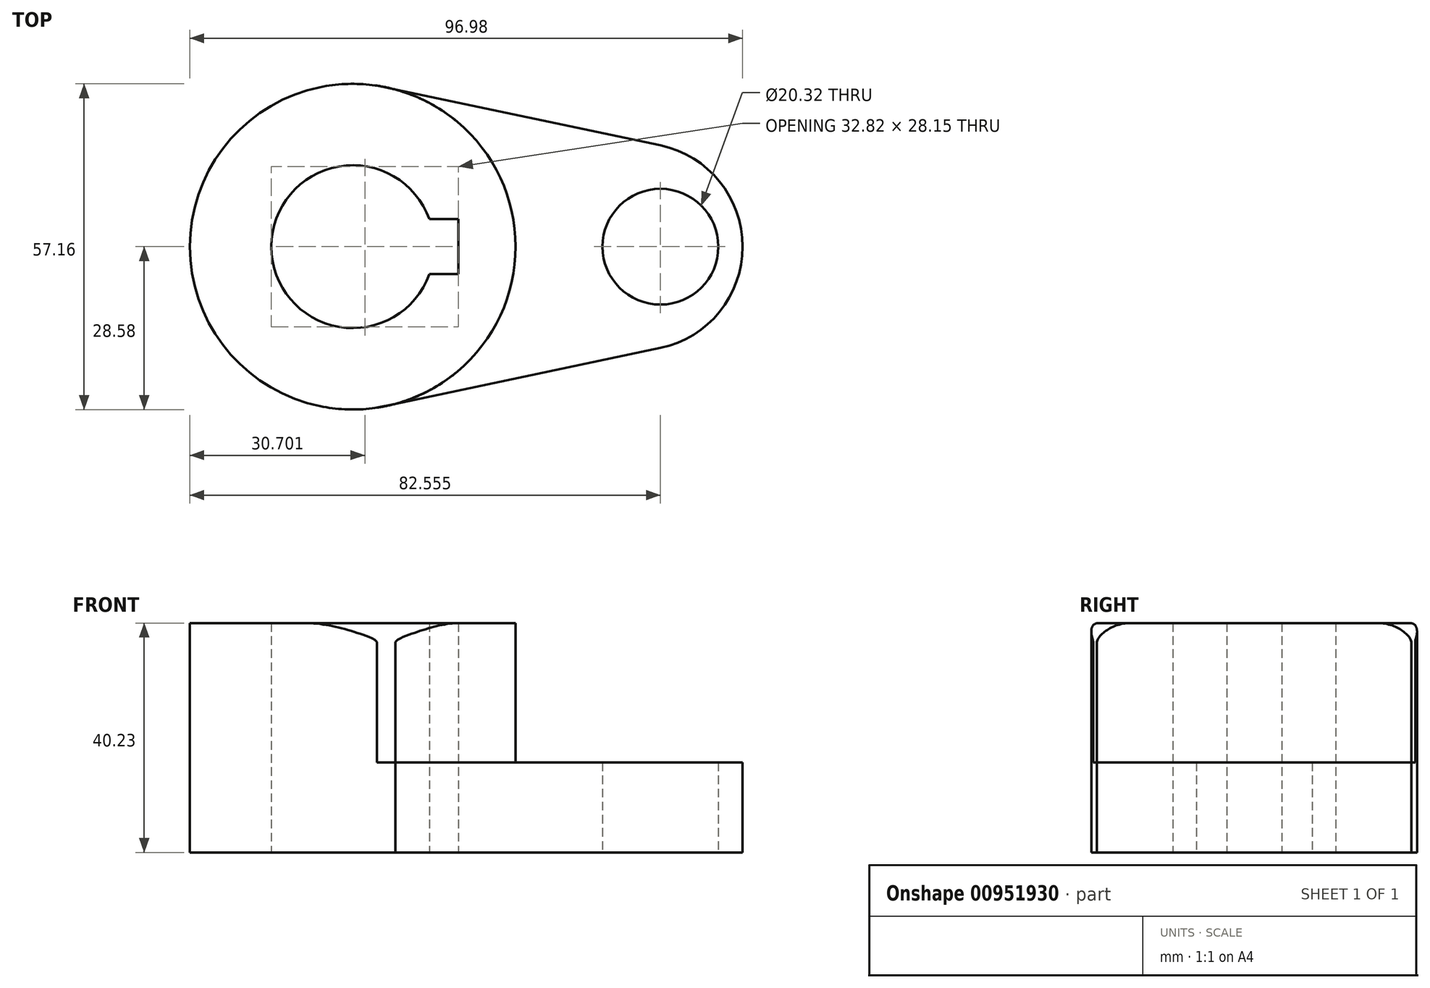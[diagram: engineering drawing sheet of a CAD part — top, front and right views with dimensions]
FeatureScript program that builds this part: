
annotation { "Feature Type Name" : "Feature", "Feature Type Description" : "" }
export const myFeature = defineFeature(function(context is Context, id is Id, definition is map)
    precondition{}
    {
        {
            var Q0;
            Q0=qCreatedBy(makeId("Top.planeOp"),FACE);
            var sketch = newSketch(context, id + "F0", { "sketchPlane" : qUnion([Q0])});
            skCircle(sketch, "E0", {"center": v(0, 0) * mm, "radius": 28.58 * mm});
            skCircle(sketch, "E1", {"center": v(53.98, 0) * mm, "radius": 10.16 * mm});
            skArc(sketch, "E2", {"start": v(13.45, 4.83) * mm, "mid": v(-14.29, 0) * mm, "end": v(13.45, -4.83) * mm});
            skLineSegment(sketch, "E3", {"start": v(4.27, -28.25) * mm, "end": v(53.97, -17.78) * mm});
            skLineSegment(sketch, "E4", {"start": v(4.27, 28.25) * mm, "end": v(53.97, 17.78) * mm});
            skArc(sketch, "E5", {"start": v(53.97, -17.78) * mm, "mid": v(68.4, 0) * mm, "end": v(53.97, 17.78) * mm});
            skLineSegment(sketch, "E6.bottom", {"start": v(13.45, -4.83) * mm, "end": v(18.53, -4.83) * mm});
            skLineSegment(sketch, "E6.top", {"start": v(13.45, 4.83) * mm, "end": v(18.53, 4.83) * mm});
            skLineSegment(sketch, "E6.right", {"start": v(18.53, -4.83) * mm, "end": v(18.53, 4.83) * mm});
            skSolve(sketch);
        }
        {
            var Q0;
            Q0=makeQuery(id+"F0.imprint","IMPRINT",FACE,{"disambiguationData":[TD([[makeQuery(id+"F0.imprint","IMPRINT",EDGE,{"derivedFrom":sQuery(id+"F0.wireOp",EDGE,"E2")}),-1.0]])]});
            extrude(context, id + "F1", {"entities" : qUnion([Q0]), "depth" : 40.23 * mm, "offsetDistance" : 25.4 * mm});
        }
        {
            var Q0;
            Q0 = qSketchRegion(id + "F0", true);
            extrude(context, id + "F2", {"entities" : qUnion([Q0]), "operationType" : NewBodyOperationType.ADD, "depth" : 15.77 * mm, "offsetDistance" : 25.4 * mm});
        }
        {
            var Q0;
            {var subQ0=sQuery(id+"F0.wireOp",EDGE,"E0");Q0=makeQuery(id+"F1.opExtrude","CAP_EDGE",EDGE,{"disambiguationData":[OSD([subQ0]),TDD([makeQuery(id+"F0.imprint","IMPRINT",EDGE,{"disambiguationData":[TD([[makeQuery(id+"F0.imprint","INTERSECT",VERTEX,{"disambiguationData":[OD(0.0)],"derivedFrom":[subQ0,sQuery(id+"F0.wireOp",EDGE,"E3")]}),1.0]])],"derivedFrom":subQ0})])],"isStart":false});}
            var Q1;
            {var subQ0=sQuery(id+"F0.wireOp",EDGE,"E0");Q1=makeQuery(id+"F1.opExtrude","CAP_EDGE",EDGE,{"disambiguationData":[OSD([subQ0]),TDD([makeQuery(id+"F0.imprint","IMPRINT",EDGE,{"disambiguationData":[TD([[makeQuery(id+"F0.imprint","INTERSECT",VERTEX,{"disambiguationData":[OD(1.0)],"derivedFrom":[subQ0,sQuery(id+"F0.wireOp",EDGE,"E4")]}),1.0]])],"derivedFrom":subQ0})])],"isStart":false});}
            var Q2;
            Q2=makeQuery(id+"F1.opExtrude","CAP_EDGE",EDGE,{"disambiguationData":[OSD([sQuery(id+"F0.wireOp",EDGE,"E3")])],"isStart":false});
            var Q3;
            Q3=makeQuery(id+"F1.opExtrude","CAP_EDGE",EDGE,{"disambiguationData":[OSD([sQuery(id+"F0.wireOp",EDGE,"E4")])],"isStart":false});
            fillet(context, id + "F3", {"entities" : qUnion([Q0, Q1, Q2, Q3]), "radius" : 3.3 * mm, "tangentPropagation" : true, "allowEdgeOverflow" : false});
        }
    });
